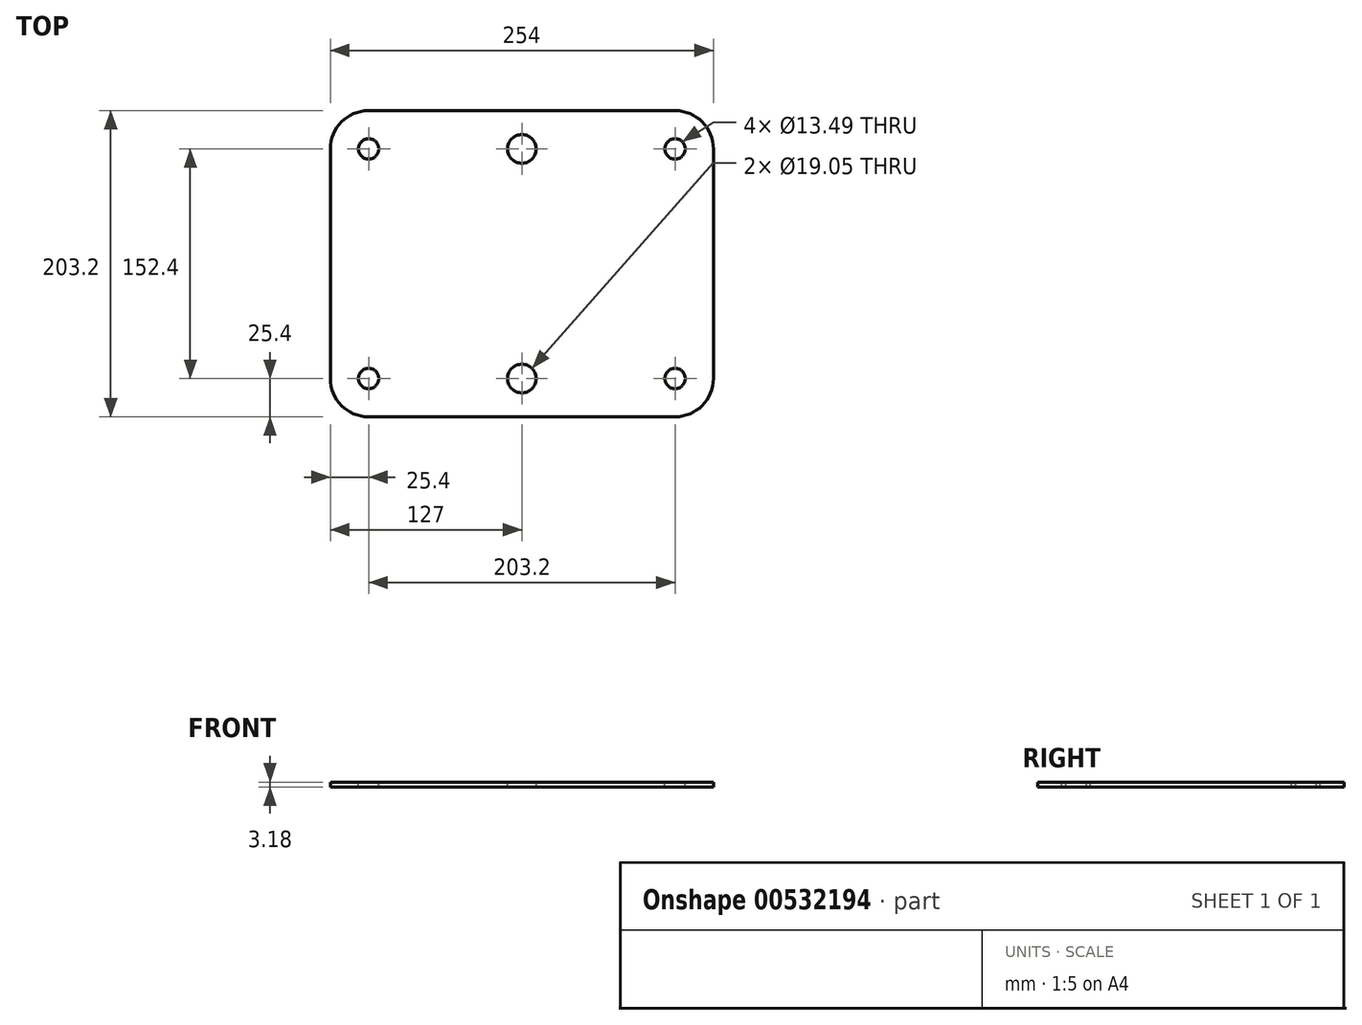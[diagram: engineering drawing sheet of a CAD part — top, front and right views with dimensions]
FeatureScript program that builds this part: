
annotation { "Feature Type Name" : "Feature", "Feature Type Description" : "" }
export const myFeature = defineFeature(function(context is Context, id is Id, definition is map)
    precondition{}
    {
        {
            var Q0;
            Q0=qCreatedBy(makeId("Top.planeOp"),FACE);
            var sketch = newSketch(context, id + "F0", { "sketchPlane" : qUnion([Q0])});
            skLineSegment(sketch, "E0.bottom", {"start": v(127, 101.6) * mm, "end": v(-127, 101.6) * mm});
            skLineSegment(sketch, "E0.top", {"start": v(127, -101.6) * mm, "end": v(-127, -101.6) * mm});
            skLineSegment(sketch, "E0.left", {"start": v(127, 101.6) * mm, "end": v(127, -101.6) * mm});
            skLineSegment(sketch, "E0.right", {"start": v(-127, 101.6) * mm, "end": v(-127, -101.6) * mm});
            skPoint(sketch, "E0.middle", {"position": v(0, 0) * mm});
            skSolve(sketch);
        }
        {
            var Q0;
            Q0 = qSketchRegion(id + "F0", true);
            extrude(context, id + "F1", {"entities" : qUnion([Q0]), "depth" : 3.17 * mm, "offsetDistance" : 25.4 * mm});
        }
        {
            var Q0;
            Q0=makeQuery(id+"F1.opExtrude","SWEPT_EDGE",EDGE,{"disambiguationData":[OSD([sQuery(id+"F0.wireOp",EDGE,"E0.bottom"),sQuery(id+"F0.wireOp",EDGE,"E0.left")])]});
            var Q1;
            Q1=makeQuery(id+"F1.opExtrude","SWEPT_EDGE",EDGE,{"disambiguationData":[OSD([sQuery(id+"F0.wireOp",EDGE,"E0.bottom"),sQuery(id+"F0.wireOp",EDGE,"E0.right")])]});
            var Q2;
            Q2=makeQuery(id+"F1.opExtrude","SWEPT_EDGE",EDGE,{"disambiguationData":[OSD([sQuery(id+"F0.wireOp",EDGE,"E0.top"),sQuery(id+"F0.wireOp",EDGE,"E0.left")])]});
            var Q3;
            Q3=makeQuery(id+"F1.opExtrude","SWEPT_EDGE",EDGE,{"disambiguationData":[OSD([sQuery(id+"F0.wireOp",EDGE,"E0.top"),sQuery(id+"F0.wireOp",EDGE,"E0.right")])]});
            fillet(context, id + "F2", {"entities" : qUnion([Q0, Q1, Q2, Q3]), "radius" : 25.4 * mm, "tangentPropagation" : true, "allowEdgeOverflow" : false});
        }
        {
            var Q0;
            Q0=makeQuery(id+"F1.opExtrude","CAP_FACE",FACE,{"disambiguationData":[OSD([sQuery(id+"F0.wireOp",EDGE,"E0.bottom"),sQuery(id+"F0.wireOp",EDGE,"E0.top"),sQuery(id+"F0.wireOp",EDGE,"E0.left"),sQuery(id+"F0.wireOp",EDGE,"E0.right")])],"isStart":false});
            var sketch = newSketch(context, id + "F3", { "sketchPlane" : qUnion([Q0])});
            skCircle(sketch, "E1", {"center": v(0, 76.2) * mm, "radius": 9.53 * mm});
            skCircle(sketch, "E2", {"center": v(0, -76.2) * mm, "radius": 9.53 * mm});
            skLineSegment(sketch, "E3.bottom", {"start": v(-101.6, 76.2) * mm, "end": v(101.6, 76.2) * mm, "construction": true});
            skLineSegment(sketch, "E3.top", {"start": v(-101.6, -76.2) * mm, "end": v(101.6, -76.2) * mm, "construction": true});
            skLineSegment(sketch, "E3.left", {"start": v(-101.6, 76.2) * mm, "end": v(-101.6, -76.2) * mm, "construction": true});
            skLineSegment(sketch, "E3.right", {"start": v(101.6, 76.2) * mm, "end": v(101.6, -76.2) * mm, "construction": true});
            skCircle(sketch, "E4", {"center": v(-101.6, 76.2) * mm, "radius": 6.75 * mm});
            skCircle(sketch, "E5", {"center": v(-101.6, -76.2) * mm, "radius": 6.75 * mm});
            skCircle(sketch, "E6", {"center": v(101.6, 76.2) * mm, "radius": 6.75 * mm});
            skCircle(sketch, "E7", {"center": v(101.6, -76.2) * mm, "radius": 6.75 * mm});
            skLineSegment(sketch, "E8", {"start": v(-127, 0) * mm, "end": v(-101.6, 0) * mm, "construction": true});
            skLineSegment(sketch, "E9", {"start": v(101.6, 0) * mm, "end": v(127, 0) * mm, "construction": true});
            skSolve(sketch);
        }
        {
            var Q0;
            Q0 = qSketchRegion(id + "F3", true);
            extrude(context, id + "F4", {"entities" : qUnion([Q0]), "operationType" : NewBodyOperationType.REMOVE, "endBound" : BoundingType.THROUGH_ALL, "oppositeDirection" : true, "depth" : 25.4 * mm, "offsetDistance" : 25.4 * mm});
        }
    });
